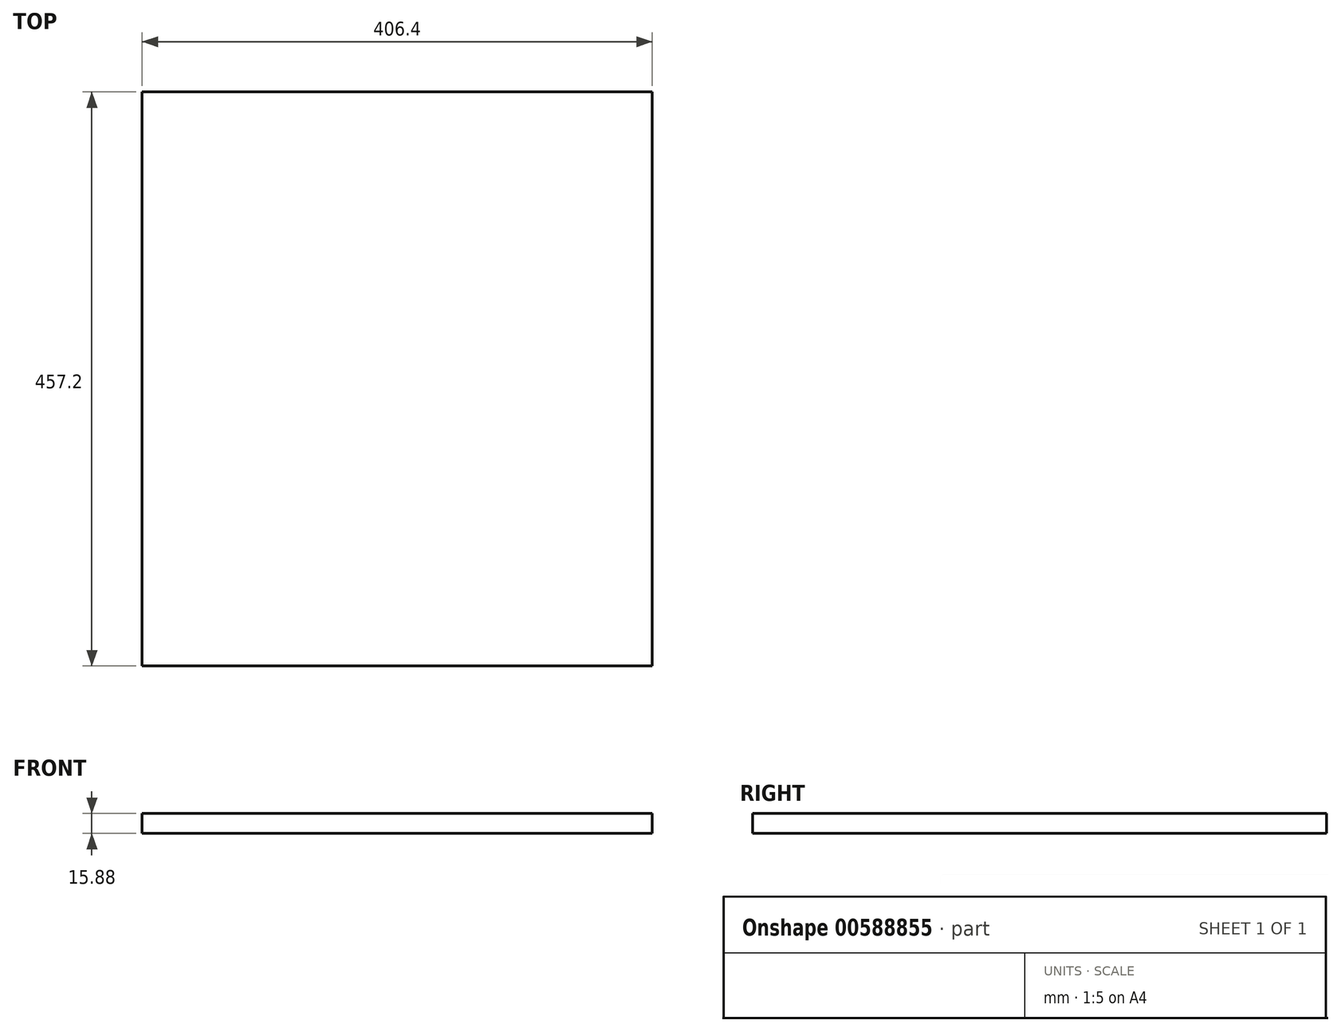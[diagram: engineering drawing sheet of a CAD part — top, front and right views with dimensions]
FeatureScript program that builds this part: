
annotation { "Feature Type Name" : "Feature", "Feature Type Description" : "" }
export const myFeature = defineFeature(function(context is Context, id is Id, definition is map)
    precondition{}
    {
        {
            var Q0;
            Q0=qCreatedBy(makeId("Top.planeOp"),FACE);
            var sketch = newSketch(context, id + "F0", { "sketchPlane" : qUnion([Q0])});
            skLineSegment(sketch, "E0.bottom", {"start": v(0, 0) * mm, "end": v(406.4, 0) * mm});
            skLineSegment(sketch, "E0.top", {"start": v(0, 457.2) * mm, "end": v(406.4, 457.2) * mm});
            skLineSegment(sketch, "E0.left", {"start": v(0, 0) * mm, "end": v(0, 457.2) * mm});
            skLineSegment(sketch, "E0.right", {"start": v(406.4, 0) * mm, "end": v(406.4, 457.2) * mm});
            skSolve(sketch);
        }
        {
            var Q0;
            Q0=makeQuery(id+"F0.imprint","IMPRINT",FACE,{"disambiguationData":[TD([[makeQuery(id+"F0.imprint","IMPRINT",EDGE,{"derivedFrom":sQuery(id+"F0.wireOp",EDGE,"E0.bottom")}),1.0]])]});
            extrude(context, id + "F1", {"entities" : qUnion([Q0]), "depth" : 15.88 * mm, "offsetDistance" : 25.4 * mm});
        }
    });
